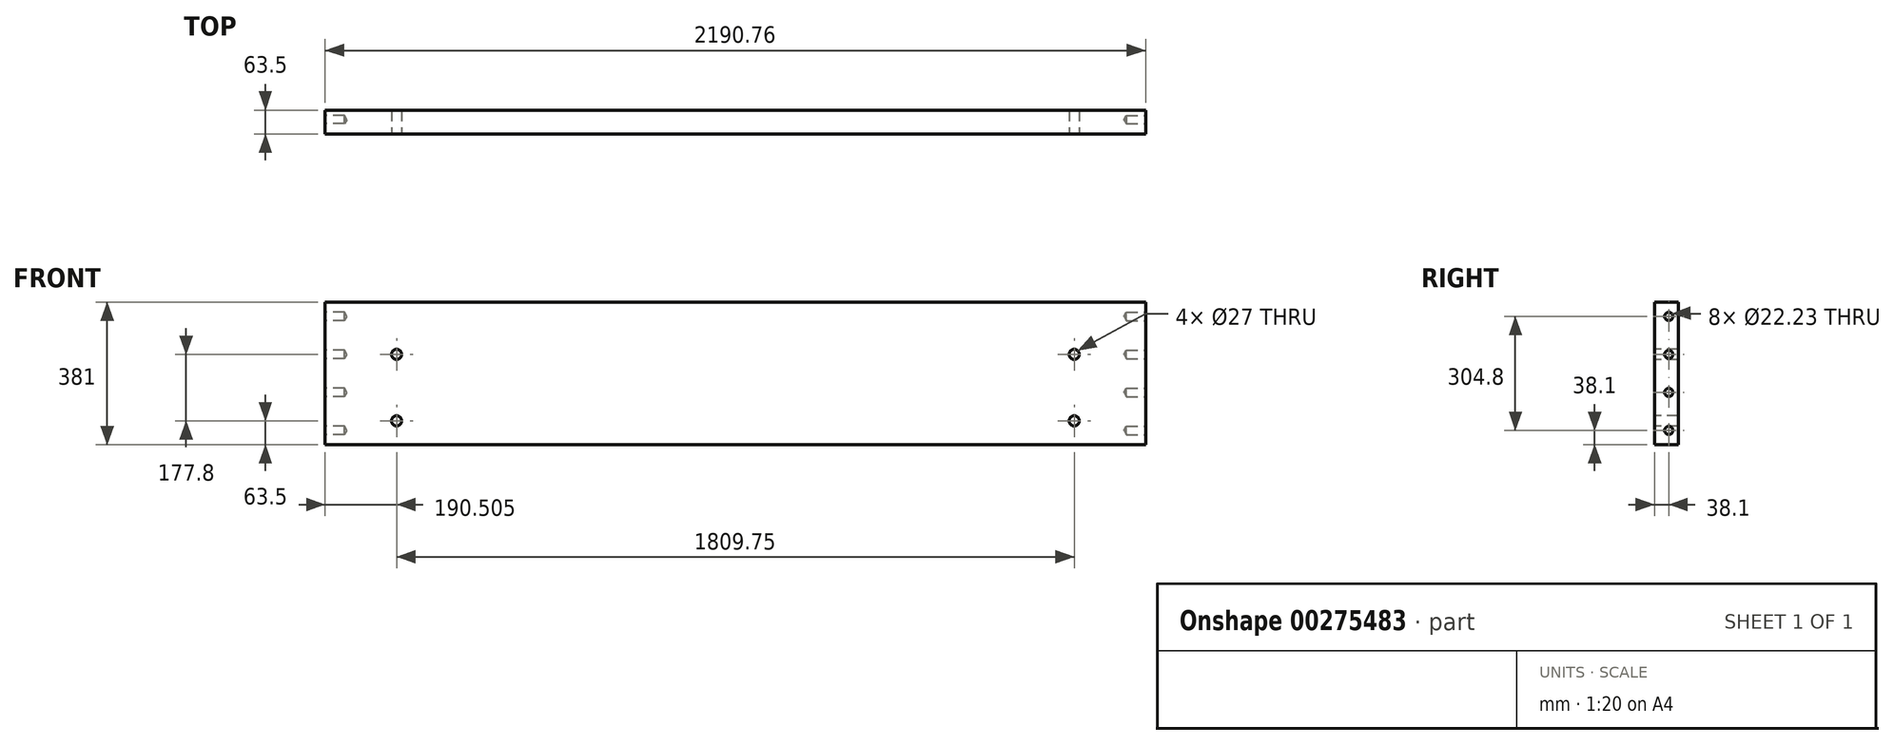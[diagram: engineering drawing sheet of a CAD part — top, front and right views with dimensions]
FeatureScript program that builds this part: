
annotation { "Feature Type Name" : "Feature", "Feature Type Description" : "" }
export const myFeature = defineFeature(function(context is Context, id is Id, definition is map)
    precondition{}
    {
        {
            var Q0;
            Q0=qCreatedBy(makeId("Right.planeOp"),FACE);
            var sketch = newSketch(context, id + "F0", { "sketchPlane" : qUnion([Q0])});
            skLineSegment(sketch, "E0.bottom", {"start": v(-31.75, 190.5) * mm, "end": v(31.75, 190.5) * mm});
            skLineSegment(sketch, "E0.top", {"start": v(-31.75, -190.5) * mm, "end": v(31.75, -190.5) * mm});
            skLineSegment(sketch, "E0.left", {"start": v(-31.75, 190.5) * mm, "end": v(-31.75, -190.5) * mm});
            skLineSegment(sketch, "E0.right", {"start": v(31.75, 190.5) * mm, "end": v(31.75, -190.5) * mm});
            skPoint(sketch, "E0.middle", {"position": v(0, 0) * mm});
            skSolve(sketch);
        }
        {
            var Q0;
            Q0 = qSketchRegion(id + "F0", true);
            extrude(context, id + "F1", {"entities" : qUnion([Q0]), "depth" : 1095.38 * mm});
        }
        {
            var Q0;
            Q0=makeQuery(id+"F1.opExtrude","CAP_FACE",FACE,{"disambiguationData":[OSD([sQuery(id+"F0.wireOp",EDGE,"E0.bottom"),sQuery(id+"F0.wireOp",EDGE,"E0.top"),sQuery(id+"F0.wireOp",EDGE,"E0.left"),sQuery(id+"F0.wireOp",EDGE,"E0.right")])],"isStart":false});
            var sketch = newSketch(context, id + "F2", { "sketchPlane" : qUnion([Q0])});
            skLineSegment(sketch, "E1.0", {"start": v(-31.75, 190.5) * mm, "end": v(-31.75, -190.5) * mm, "construction": true});
            skLineSegment(sketch, "E2.0", {"start": v(6.35, 190.5) * mm, "end": v(6.35, -190.5) * mm, "construction": true});
            skLineSegment(sketch, "E3.0", {"start": v(-31.75, 152.4) * mm, "end": v(31.75, 152.4) * mm, "construction": true});
            skPoint(sketch, "E4", {"position": v(6.35, 152.4) * mm});
            skPoint(sketch, "E5.0.1.0", {"position": v(6.35, 50.8) * mm});
            skPoint(sketch, "E5.0.2.0", {"position": v(6.35, -50.8) * mm});
            skPoint(sketch, "E5.0.3.0", {"position": v(6.35, -152.4) * mm});
            skLineSegment(sketch, "E5.direction1", {"start": v(6.35, 152.4) * mm, "end": v(31.75, 152.4) * mm, "construction": true});
            skLineSegment(sketch, "E5.direction2", {"start": v(6.35, 152.4) * mm, "end": v(6.35, 50.8) * mm, "construction": true});
            skSolve(sketch);
        }
        {
            var Q0;
            Q0=sQuery(id+"F2.wireOp",VERTEX,"E4");
            var Q1;
            Q1=sQuery(id+"F2.wireOp",VERTEX,"E5.0.1.0");
            var Q2;
            Q2=sQuery(id+"F2.wireOp",VERTEX,"E5.0.2.0");
            var Q3;
            Q3=sQuery(id+"F2.wireOp",VERTEX,"E5.0.3.0");
            var Q4;
            Q4=makeQuery(id+"F1.opExtrude","SWEPT_BODY",BODY,{"disambiguationData":[OSD([sQuery(id+"F0.wireOp",EDGE,"E0.bottom"),sQuery(id+"F0.wireOp",EDGE,"E0.top"),sQuery(id+"F0.wireOp",EDGE,"E0.left"),sQuery(id+"F0.wireOp",EDGE,"E0.right")])]});
            hole(context, id + "F3", {"style" : HoleStyle.SIMPLE, "endStyle" : HoleEndStyle.BLIND, "standardTappedOrClearance" : lookupTablePath({ "standard" : "ANSI", "engagement" : "75%", "pitch" : "8 tpi", "size" : "1", "type" : "Tapped" }), "standardBlindInLast" : lookupTablePath({ "standard" : "ANSI", "engagement" : "75%", "pitch" : "8 tpi", "size" : "1", "type" : "Tapped" }), "holeDiameter" : 22.22 * mm, "showTappedDepth" : true, "holeDepth" : 50.8 * mm, "tappedDepth" : 41.27 * mm, "tapClearance" : 3, "startFromSketch" : true, "locations" : qUnion([Q0, Q1, Q2, Q3]), "scope" : qUnion([Q4]), "majorDiameter" : 25.4 * mm});
        }
        {
            var Q0;
            Q0=makeQuery(id+"F1.opExtrude","SWEPT_FACE",FACE,{"disambiguationData":[OSD([sQuery(id+"F0.wireOp",EDGE,"E0.left")])]});
            var sketch = newSketch(context, id + "F4", { "sketchPlane" : qUnion([Q0])});
            skLineSegment(sketch, "E6.0", {"start": v(904.88, 190.5) * mm, "end": v(904.88, -190.5) * mm, "construction": true});
            skLineSegment(sketch, "E7.0", {"start": v(1095.38, -127) * mm, "end": v(0, -127) * mm, "construction": true});
            skLineSegment(sketch, "E8.0", {"start": v(1095.38, 50.8) * mm, "end": v(0, 50.8) * mm, "construction": true});
            skPoint(sketch, "E9", {"position": v(904.88, 50.8) * mm});
            skPoint(sketch, "E10", {"position": v(904.88, -127) * mm});
            skSolve(sketch);
        }
        {
            var Q0;
            Q0=sQuery(id+"F4.wireOp",VERTEX,"E9");
            var Q1;
            Q1=sQuery(id+"F4.wireOp",VERTEX,"E10");
            var Q2;
            Q2=makeQuery(id+"F1.opExtrude","SWEPT_BODY",BODY,{"disambiguationData":[OSD([sQuery(id+"F0.wireOp",EDGE,"E0.bottom"),sQuery(id+"F0.wireOp",EDGE,"E0.top"),sQuery(id+"F0.wireOp",EDGE,"E0.left"),sQuery(id+"F0.wireOp",EDGE,"E0.right")])]});
            hole(context, id + "F5", {"style" : HoleStyle.SIMPLE, "endStyle" : HoleEndStyle.THROUGH, "holeDiameter" : 27 * mm, "tappedDepth" : 41.27 * mm, "tapClearance" : 3, "startFromSketch" : true, "locations" : qUnion([Q0, Q1]), "scope" : qUnion([Q2])});
        }
        {
            var Q0;
            Q0=makeQuery(id+"F1.opExtrude","SWEPT_BODY",BODY,{"disambiguationData":[OSD([sQuery(id+"F0.wireOp",EDGE,"E0.bottom"),sQuery(id+"F0.wireOp",EDGE,"E0.top"),sQuery(id+"F0.wireOp",EDGE,"E0.left"),sQuery(id+"F0.wireOp",EDGE,"E0.right")])]});
            var Q1;
            Q1=qCreatedBy(makeId("Right.planeOp"),FACE);
            mirror(context, id + "F6", {"operationType" : NewBodyOperationType.ADD, "entities" : qUnion([Q0]), "mirrorPlane" : qUnion([Q1])});
        }
    });
